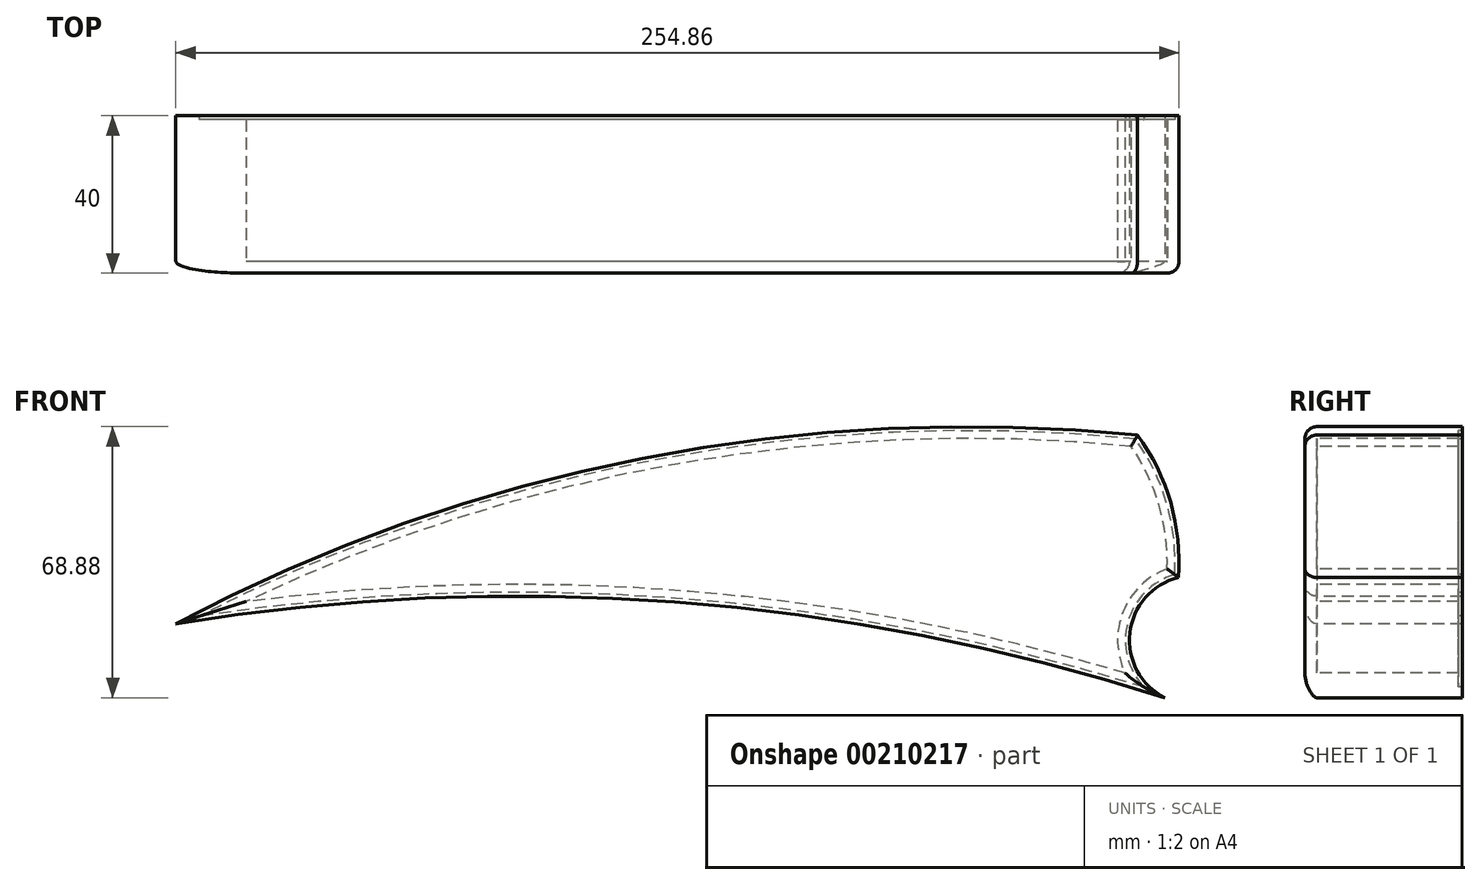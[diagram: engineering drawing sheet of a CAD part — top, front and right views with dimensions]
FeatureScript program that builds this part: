
annotation { "Feature Type Name" : "Feature", "Feature Type Description" : "" }
export const myFeature = defineFeature(function(context is Context, id is Id, definition is map)
    precondition{}
    {
        {
            var Q0;
            Q0=qCreatedBy(makeId("Front.planeOp"),FACE);
            var sketch = newSketch(context, id + "F0", { "sketchPlane" : qUnion([Q0])});
            skArc(sketch, "E0", {"start": v(87.4, 39.46) * mm, "mid": v(-27.69, 35.01) * mm, "end": v(-137.4, 0) * mm});
            skArc(sketch, "E1", {"start": v(85.86, -18.17) * mm, "mid": v(-24.82, 2.6) * mm, "end": v(-137.4, 0) * mm});
            skArc(sketch, "E2", {"start": v(96.54, 8.36) * mm, "mid": v(85.37, -2.56) * mm, "end": v(85.86, -18.17) * mm});
            skArc(sketch, "E3", {"start": v(96.54, 8.36) * mm, "mid": v(94.48, 24.64) * mm, "end": v(87.4, 39.46) * mm});
            skArc(sketch, "E4.0", {"start": v(99.43, 6.12) * mm, "mid": v(97.46, 25.14) * mm, "end": v(89.05, 42.3) * mm});
            skArc(sketch, "E4.1", {"start": v(99.43, 6.12) * mm, "mid": v(87.07, -7.95) * mm, "end": v(95.95, -24.43) * mm});
            skArc(sketch, "E4.2", {"start": v(95.95, -24.43) * mm, "mid": v(-28.56, -0.12) * mm, "end": v(-155.3, -5.63) * mm});
            skArc(sketch, "E4.3", {"start": v(89.05, 42.3) * mm, "mid": v(-36.67, 36.4) * mm, "end": v(-155.3, -5.63) * mm});
            skArc(sketch, "E5.0", {"start": v(98.48, 6.9) * mm, "mid": v(86.58, -5.24) * mm, "end": v(90.7, -21.72) * mm});
            skArc(sketch, "E5.1", {"start": v(98.48, 6.9) * mm, "mid": v(96.46, 24.99) * mm, "end": v(88.5, 41.36) * mm});
            skArc(sketch, "E5.2", {"start": v(88.5, 41.36) * mm, "mid": v(-33.7, 35.95) * mm, "end": v(-149.4, -3.7) * mm});
            skArc(sketch, "E5.3", {"start": v(90.7, -21.72) * mm, "mid": v(-28.34, 0.87) * mm, "end": v(-149.4, -3.7) * mm});
            skSolve(sketch);
        }
        {
            var Q0;
            Q0=makeQuery(id+"F0.imprint","IMPRINT",FACE,{"disambiguationData":[TD([[makeQuery(id+"F0.imprint","IMPRINT",EDGE,{"derivedFrom":sQuery(id+"F0.wireOp",EDGE,"E0")}),-1.0]])]});
            extrude(context, id + "F1", {"entities" : qUnion([Q0]), "depth" : 39 * mm});
        }
        {
            var Q0;
            Q0=makeQuery(id+"F0.imprint","IMPRINT",FACE,{"disambiguationData":[TD([[makeQuery(id+"F0.imprint","IMPRINT",EDGE,{"derivedFrom":sQuery(id+"F0.wireOp",EDGE,"E0")}),1.0]])]});
            extrude(context, id + "F2", {"entities" : qUnion([Q0]), "operationType" : NewBodyOperationType.ADD, "depth" : 3 * mm});
        }
        {
            var Q0;
            Q0=makeQuery(id+"F0.imprint","IMPRINT",FACE,{"disambiguationData":[TD([[makeQuery(id+"F0.imprint","IMPRINT",EDGE,{"derivedFrom":sQuery(id+"F0.wireOp",EDGE,"E4.0")}),1.0]])]});
            extrude(context, id + "F3", {"entities" : qUnion([Q0]), "operationType" : NewBodyOperationType.ADD, "depth" : 40 * mm});
        }
        {
            var Q0;
            Q0=makeQuery(id+"F3.opExtrude","CAP_EDGE",EDGE,{"disambiguationData":[OSD([sQuery(id+"F0.wireOp",EDGE,"E4.3")])],"isStart":true});
            var Q1;
            Q1=makeQuery(id+"F3.opExtrude","CAP_EDGE",EDGE,{"disambiguationData":[OSD([sQuery(id+"F0.wireOp",EDGE,"E4.2")])],"isStart":true});
            var Q2;
            Q2=makeQuery(id+"F3.opExtrude","CAP_EDGE",EDGE,{"disambiguationData":[OSD([sQuery(id+"F0.wireOp",EDGE,"E4.1")])],"isStart":true});
            var Q3;
            Q3=makeQuery(id+"F3.opExtrude","CAP_EDGE",EDGE,{"disambiguationData":[OSD([sQuery(id+"F0.wireOp",EDGE,"E4.0")])],"isStart":true});
            fillet(context, id + "F4", {"entities" : qUnion([Q0, Q1, Q2, Q3]), "radius" : 3 * mm, "tangentPropagation" : true, "allowEdgeOverflow" : false});
        }
        {
            var Q0;
            Q0=makeQuery(id+"F1.opExtrude","SWEPT_BODY",BODY,{"disambiguationData":[OSD([sQuery(id+"F0.wireOp",EDGE,"E0"),sQuery(id+"F0.wireOp",EDGE,"E1"),sQuery(id+"F0.wireOp",EDGE,"E2"),sQuery(id+"F0.wireOp",EDGE,"E3"),sQuery(id+"F0.wireOp",EDGE,"E5.0"),sQuery(id+"F0.wireOp",EDGE,"E5.1"),sQuery(id+"F0.wireOp",EDGE,"E5.2"),sQuery(id+"F0.wireOp",EDGE,"E5.3")])]});
            var Q1;
            Q1=qNothing();
            var Q2;
            Q2=qCreatedBy(makeId("Front.planeOp"),FACE);
            mirror(context, id + "F5", {"entities" : qUnion([Q0, Q1]), "mirrorPlane" : qUnion([Q2])});
        }
        {
            var Q0;
            Q0=makeQuery(id+"F1.opExtrude","SWEPT_BODY",BODY,{"disambiguationData":[OSD([sQuery(id+"F0.wireOp",EDGE,"E0"),sQuery(id+"F0.wireOp",EDGE,"E1"),sQuery(id+"F0.wireOp",EDGE,"E2"),sQuery(id+"F0.wireOp",EDGE,"E3"),sQuery(id+"F0.wireOp",EDGE,"E5.0"),sQuery(id+"F0.wireOp",EDGE,"E5.1"),sQuery(id+"F0.wireOp",EDGE,"E5.2"),sQuery(id+"F0.wireOp",EDGE,"E5.3")])]});
            deleteBodies(context, id + "F6", {"entities" : qUnion([Q0])});
        }
    });
